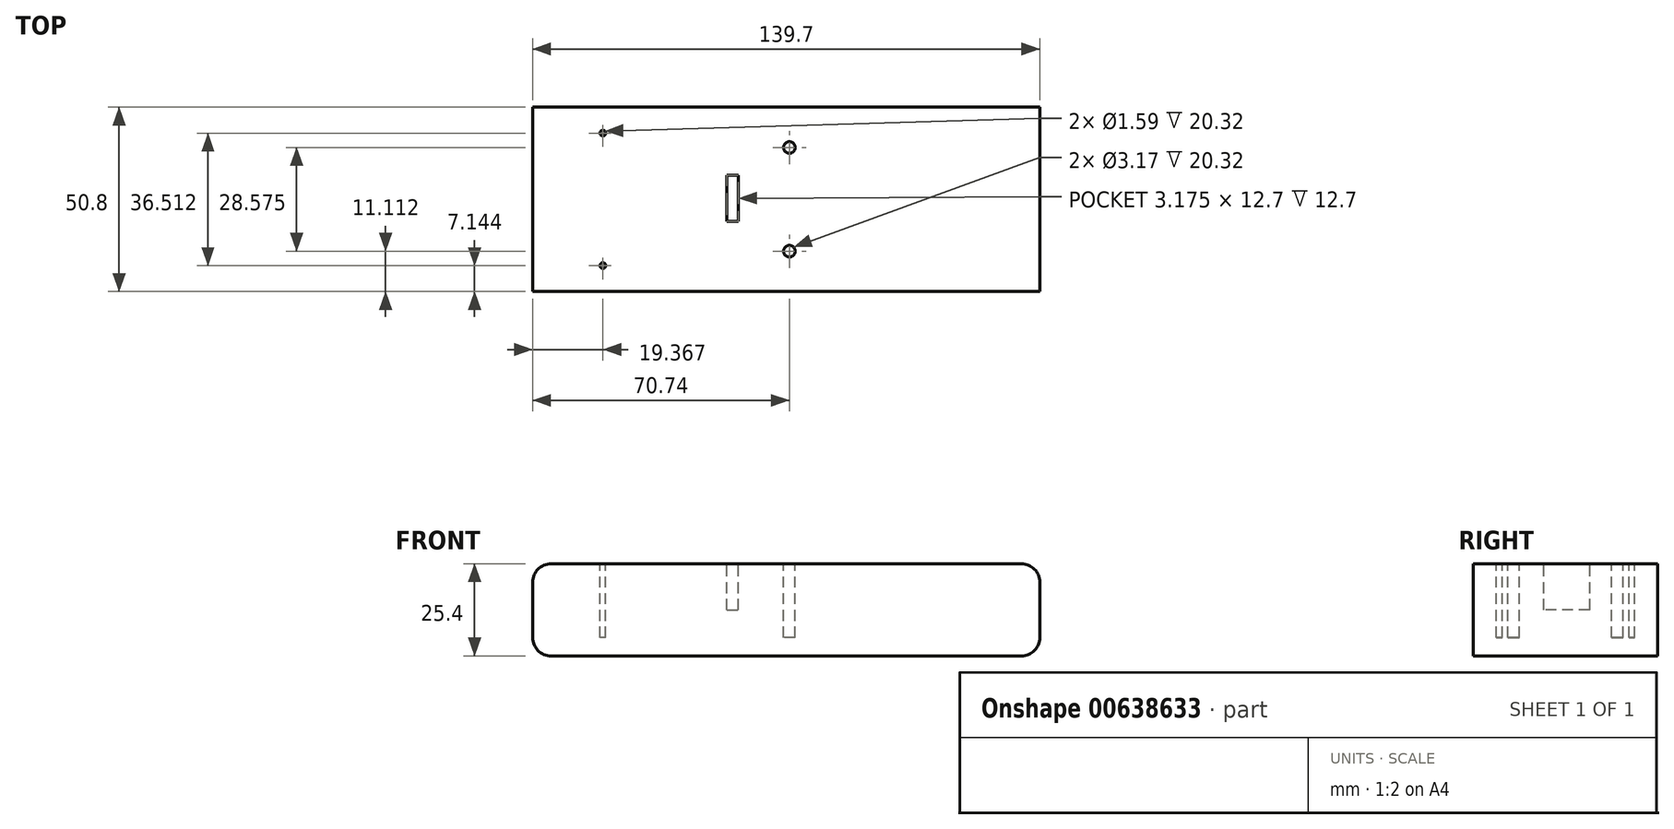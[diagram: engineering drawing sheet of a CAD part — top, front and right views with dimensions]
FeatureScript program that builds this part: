
annotation { "Feature Type Name" : "Feature", "Feature Type Description" : "" }
export const myFeature = defineFeature(function(context is Context, id is Id, definition is map)
    precondition{}
    {
        {
            var Q0;
            Q0=qCreatedBy(makeId("Front.planeOp"),FACE);
            var sketch = newSketch(context, id + "F0", { "sketchPlane" : qUnion([Q0])});
            skLineSegment(sketch, "E0", {"start": v(-70.74, 11.32) * mm, "end": v(68.96, 11.32) * mm});
            skLineSegment(sketch, "E1", {"start": v(68.96, 11.32) * mm, "end": v(68.96, -14.08) * mm});
            skLineSegment(sketch, "E2", {"start": v(68.96, -14.08) * mm, "end": v(-70.74, -14.08) * mm});
            skLineSegment(sketch, "E3", {"start": v(-70.74, -14.08) * mm, "end": v(-70.74, 11.32) * mm});
            skSolve(sketch);
        }
        {
            var Q0;
            Q0 = qSketchRegion(id + "F0", true);
            extrude(context, id + "F1", {"entities" : qUnion([Q0]), "depth" : 50.8 * mm, "offsetDistance" : 25.4 * mm});
        }
        {
            var Q0;
            Q0=makeQuery(id+"F1.opExtrude","SWEPT_EDGE",EDGE,{"disambiguationData":[OSD([sQuery(id+"F0.wireOp",EDGE,"E0"),sQuery(id+"F0.wireOp",EDGE,"E3")])]});
            var Q1;
            Q1=makeQuery(id+"F1.opExtrude","SWEPT_EDGE",EDGE,{"disambiguationData":[OSD([sQuery(id+"F0.wireOp",EDGE,"E2"),sQuery(id+"F0.wireOp",EDGE,"E3")])]});
            var Q2;
            Q2=makeQuery(id+"F1.opExtrude","SWEPT_EDGE",EDGE,{"disambiguationData":[OSD([sQuery(id+"F0.wireOp",EDGE,"E0"),sQuery(id+"F0.wireOp",EDGE,"E1")])]});
            var Q3;
            Q3=makeQuery(id+"F1.opExtrude","SWEPT_EDGE",EDGE,{"disambiguationData":[OSD([sQuery(id+"F0.wireOp",EDGE,"E1"),sQuery(id+"F0.wireOp",EDGE,"E2")])]});
            fillet(context, id + "F2", {"entities" : qUnion([Q0, Q1, Q2, Q3]), "radius" : 5.08 * mm, "tangentPropagation" : true, "allowEdgeOverflow" : false});
        }
        {
            var Q0;
            Q0=makeQuery(id+"F1.opExtrude","SWEPT_FACE",FACE,{"disambiguationData":[OSD([sQuery(id+"F0.wireOp",EDGE,"E0")])]});
            var sketch = newSketch(context, id + "F3", { "sketchPlane" : qUnion([Q0])});
            skCircle(sketch, "E4", {"center": v(-51.37, -7.14) * mm, "radius": 0.8 * mm});
            skCircle(sketch, "E5", {"center": v(-51.37, -43.66) * mm, "radius": 0.8 * mm});
            skSolve(sketch);
        }
        {
            var Q0;
            Q0 = qSketchRegion(id + "F3", true);
            extrude(context, id + "F4", {"entities" : qUnion([Q0]), "operationType" : NewBodyOperationType.REMOVE, "oppositeDirection" : true, "depth" : 20.32 * mm, "offsetDistance" : 25.4 * mm});
        }
        {
            var Q0;
            Q0=makeQuery(id+"F1.opExtrude","SWEPT_FACE",FACE,{"disambiguationData":[OSD([sQuery(id+"F0.wireOp",EDGE,"E0")])]});
            var sketch = newSketch(context, id + "F5", { "sketchPlane" : qUnion([Q0])});
            skLineSegment(sketch, "E6.bottom", {"start": v(-17.2, -18.73) * mm, "end": v(-14.03, -18.73) * mm});
            skLineSegment(sketch, "E6.top", {"start": v(-17.2, -31.43) * mm, "end": v(-14.03, -31.43) * mm});
            skLineSegment(sketch, "E6.left", {"start": v(-17.2, -18.73) * mm, "end": v(-17.2, -31.43) * mm});
            skLineSegment(sketch, "E6.right", {"start": v(-14.03, -18.73) * mm, "end": v(-14.03, -31.43) * mm});
            skSolve(sketch);
        }
        {
            var Q0;
            Q0 = qSketchRegion(id + "F5", true);
            extrude(context, id + "F6", {"entities" : qUnion([Q0]), "operationType" : NewBodyOperationType.REMOVE, "oppositeDirection" : true, "depth" : 12.7 * mm, "offsetDistance" : 25.4 * mm});
        }
        {
            var Q0;
            Q0=makeQuery(id+"F1.opExtrude","SWEPT_FACE",FACE,{"disambiguationData":[OSD([sQuery(id+"F0.wireOp",EDGE,"E0")])]});
            var sketch = newSketch(context, id + "F7", { "sketchPlane" : qUnion([Q0])});
            skCircle(sketch, "E7", {"center": v(0, -11.11) * mm, "radius": 1.59 * mm});
            skCircle(sketch, "E8", {"center": v(0, -39.69) * mm, "radius": 1.59 * mm});
            skSolve(sketch);
        }
        {
            var Q0;
            Q0 = qSketchRegion(id + "F7", true);
            extrude(context, id + "F8", {"entities" : qUnion([Q0]), "operationType" : NewBodyOperationType.REMOVE, "oppositeDirection" : true, "depth" : 20.32 * mm, "offsetDistance" : 25.4 * mm});
        }
    });
